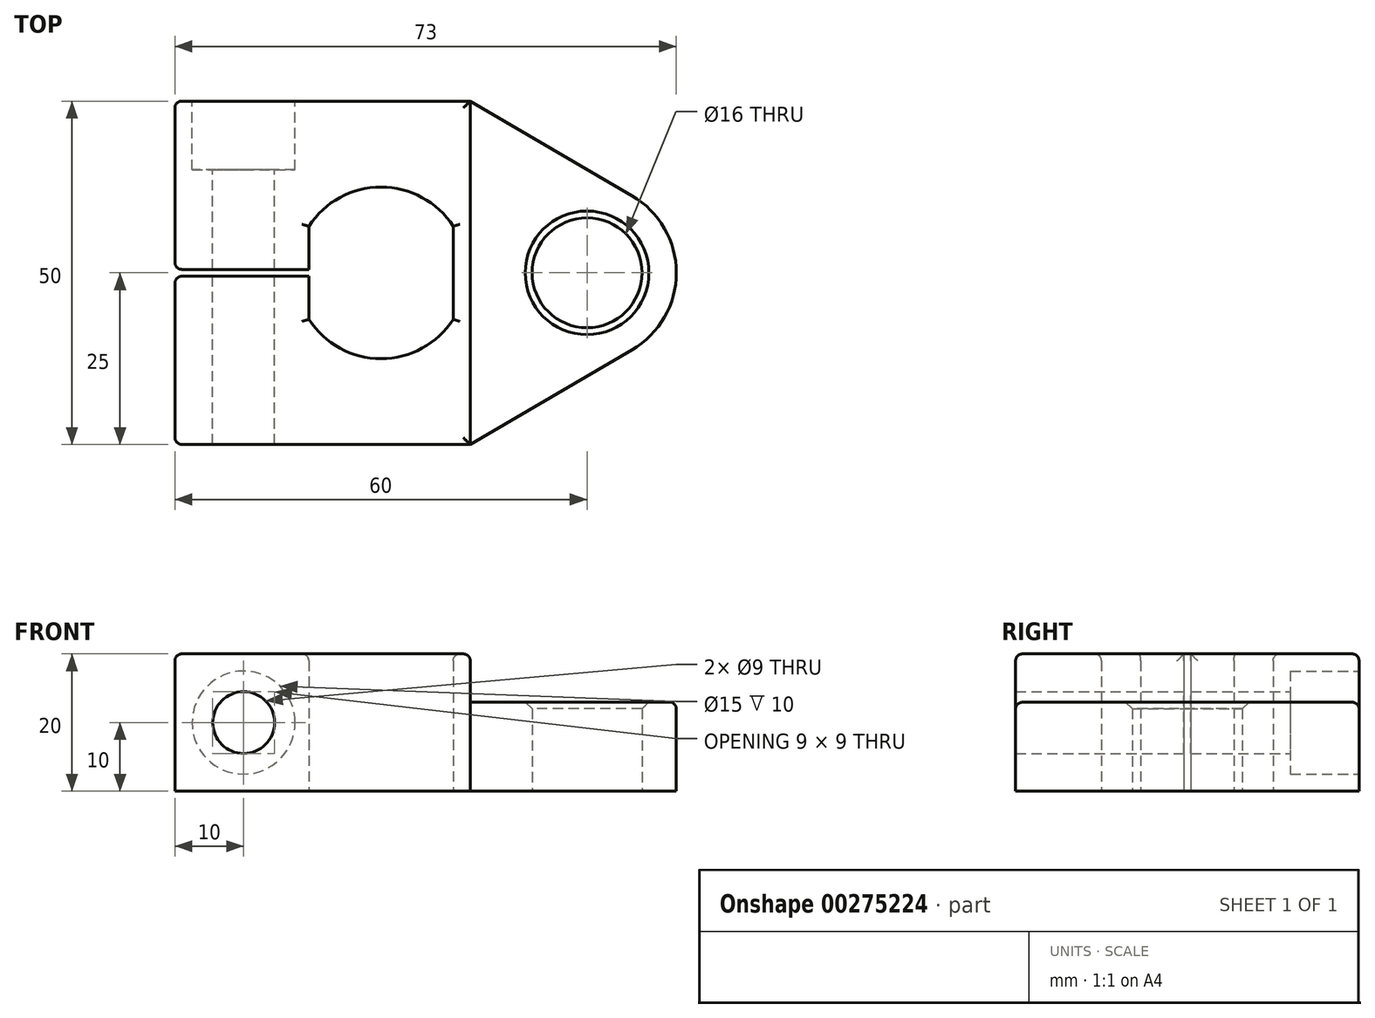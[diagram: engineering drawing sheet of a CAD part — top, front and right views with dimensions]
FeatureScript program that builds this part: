
annotation { "Feature Type Name" : "Feature", "Feature Type Description" : "" }
export const myFeature = defineFeature(function(context is Context, id is Id, definition is map)
    precondition{}
    {
        {
            var Q0;
            Q0=qCreatedBy(makeId("Top.planeOp"),FACE);
            var sketch = newSketch(context, id + "F0", { "sketchPlane" : qUnion([Q0])});
            skLineSegment(sketch, "E0", {"start": v(0, 0) * mm, "end": v(43, 0) * mm});
            skLineSegment(sketch, "E1", {"start": v(0, 0) * mm, "end": v(0, 24.5) * mm});
            skLineSegment(sketch, "E2", {"start": v(0, 50) * mm, "end": v(43, 50) * mm});
            skLineSegment(sketch, "E3", {"start": v(43, 50) * mm, "end": v(66.56, 36.22) * mm});
            skLineSegment(sketch, "E4", {"start": v(43, 0) * mm, "end": v(66.56, 13.78) * mm});
            skCircle(sketch, "E5", {"center": v(60, 25) * mm, "radius": 8 * mm});
            skArc(sketch, "E6", {"start": v(66.56, 36.22) * mm, "mid": v(73, 25) * mm, "end": v(66.56, 13.78) * mm});
            skPoint(sketch, "E7", {"position": v(73, 25) * mm});
            skLineSegment(sketch, "E8", {"start": v(43, 50) * mm, "end": v(43, 0) * mm});
            skLineSegment(sketch, "E9", {"start": v(19.5, 31.78) * mm, "end": v(19.5, 25) * mm});
            skLineSegment(sketch, "E10", {"start": v(40.5, 31.78) * mm, "end": v(40.5, 18.22) * mm});
            skArc(sketch, "E11", {"start": v(40.5, 31.78) * mm, "mid": v(30, 37.5) * mm, "end": v(19.5, 31.78) * mm});
            skLineSegment(sketch, "E12", {"start": v(60, 25) * mm, "end": v(-29.37, 25) * mm, "construction": true});
            skArc(sketch, "E13.MirrorCS", {"start": v(40.5, 18.22) * mm, "mid": v(30, 12.5) * mm, "end": v(19.5, 18.22) * mm});
            skLineSegment(sketch, "E14", {"start": v(19.5, 25.5) * mm, "end": v(0, 25.5) * mm});
            skLineSegment(sketch, "E15.MirrorCS", {"start": v(19.5, 24.5) * mm, "end": v(0, 24.5) * mm});
            skLineSegment(sketch, "E16.trimOffspring", {"start": v(0, 25) * mm, "end": v(0, 50) * mm});
            skLineSegment(sketch, "E17.trimOffspring", {"start": v(19.5, 24.5) * mm, "end": v(19.5, 18.22) * mm});
            skSolve(sketch);
        }
        {
            var Q0;
            Q0=makeQuery(id+"F0.imprint","IMPRINT",FACE,{"disambiguationData":[TD([[makeQuery(id+"F0.imprint","IMPRINT",EDGE,{"derivedFrom":sQuery(id+"F0.wireOp",EDGE,"E3")}),-1.0]])]});
            extrude(context, id + "F1", {"entities" : qUnion([Q0]), "depth" : 13 * mm});
        }
        {
            var Q0;
            Q0=makeQuery(id+"F0.imprint","IMPRINT",FACE,{"disambiguationData":[TD([[makeQuery(id+"F0.imprint","IMPRINT",EDGE,{"derivedFrom":sQuery(id+"F0.wireOp",EDGE,"E0")}),1.0]])]});
            extrude(context, id + "F2", {"entities" : qUnion([Q0]), "operationType" : NewBodyOperationType.ADD, "depth" : 20 * mm});
        }
        {
            var Q0;
            Q0=makeQuery(id+"F2.opExtrude","SWEPT_FACE",FACE,{"disambiguationData":[OSD([sQuery(id+"F0.wireOp",EDGE,"E2")])]});
            var sketch = newSketch(context, id + "F3", { "sketchPlane" : qUnion([Q0])});
            skPoint(sketch, "E18", {"position": v(-10, 10) * mm});
            skSolve(sketch);
        }
        {
            var Q0;
            Q0=sQuery(id+"F3.wireOp",VERTEX,"E18");
            var Q1;
            Q1=makeQuery(id+"F1.opExtrude","SWEPT_BODY",BODY,{"disambiguationData":[OSD([sQuery(id+"F0.wireOp",EDGE,"E3"),sQuery(id+"F0.wireOp",EDGE,"E4"),sQuery(id+"F0.wireOp",EDGE,"E5"),sQuery(id+"F0.wireOp",EDGE,"E6"),sQuery(id+"F0.wireOp",EDGE,"E8")])]});
            hole(context, id + "F4", {"style" : HoleStyle.C_BORE, "endStyle" : HoleEndStyle.THROUGH, "holeDiameter" : 9 * mm, "cBoreDiameter" : 15 * mm, "cBoreDepth" : 10 * mm, "tappedDepth" : 12 * mm, "tapClearance" : 3, "locations" : qUnion([Q0]), "scope" : qUnion([Q1])});
        }
        {
            var Q0;
            Q0=makeQuery(id+"F2.opExtrude","SWEPT_EDGE",EDGE,{"disambiguationData":[OSD([sQuery(id+"F0.wireOp",EDGE,"E0"),sQuery(id+"F0.wireOp",EDGE,"E1")])]});
            var Q1;
            Q1=makeQuery(id+"F2.opExtrude","CAP_EDGE",EDGE,{"disambiguationData":[OSD([sQuery(id+"F0.wireOp",EDGE,"E2")])],"isStart":false});
            var Q2;
            Q2=makeQuery(id+"F2.opExtrude","CAP_EDGE",EDGE,{"disambiguationData":[OSD([sQuery(id+"F0.wireOp",EDGE,"E16.trimOffspring")])],"isStart":false});
            var Q3;
            Q3=makeQuery(id+"F2.opExtrude","CAP_EDGE",EDGE,{"disambiguationData":[OSD([sQuery(id+"F0.wireOp",EDGE,"E0")])],"isStart":false});
            var Q4;
            Q4=makeQuery(id+"F2.opExtrude","CAP_EDGE",EDGE,{"disambiguationData":[OSD([sQuery(id+"F0.wireOp",EDGE,"E8")])],"isStart":false});
            var Q5;
            Q5=makeQuery(id+"F2.opExtrude","CAP_EDGE",EDGE,{"disambiguationData":[OSD([sQuery(id+"F0.wireOp",EDGE,"E11")])],"isStart":false});
            var Q6;
            Q6=makeQuery(id+"F2.opExtrude","CAP_EDGE",EDGE,{"disambiguationData":[OSD([sQuery(id+"F0.wireOp",EDGE,"E13.MirrorCS")])],"isStart":false});
            var Q7;
            Q7=makeQuery(id+"F2.opExtrude","CAP_EDGE",EDGE,{"disambiguationData":[OSD([sQuery(id+"F0.wireOp",EDGE,"E10")])],"isStart":false});
            var Q8;
            Q8=makeQuery(id+"F2.opExtrude","CAP_EDGE",EDGE,{"disambiguationData":[OSD([sQuery(id+"F0.wireOp",EDGE,"E17.trimOffspring")])],"isStart":false});
            var Q9;
            Q9=makeQuery(id+"F2.opExtrude","CAP_EDGE",EDGE,{"disambiguationData":[OSD([sQuery(id+"F0.wireOp",EDGE,"E9")])],"isStart":false});
            var Q10;
            Q10=makeQuery(id+"F2.opExtrude","SWEPT_EDGE",EDGE,{"disambiguationData":[OSD([sQuery(id+"F0.wireOp",EDGE,"E14"),sQuery(id+"F0.wireOp",EDGE,"E16.trimOffspring")])]});
            var Q11;
            Q11=makeQuery(id+"F1.opExtrude","CAP_EDGE",EDGE,{"disambiguationData":[OSD([sQuery(id+"F0.wireOp",EDGE,"E4")])],"isStart":false});
            var Q12;
            Q12=makeQuery(id+"F2.opExtrude","CAP_EDGE",EDGE,{"disambiguationData":[OSD([sQuery(id+"F0.wireOp",EDGE,"E1")])],"isStart":false});
            var Q13;
            Q13=makeQuery(id+"F2.opExtrude","SWEPT_EDGE",EDGE,{"disambiguationData":[OSD([sQuery(id+"F0.wireOp",EDGE,"E1"),sQuery(id+"F0.wireOp",EDGE,"E15.MirrorCS")])]});
            var Q14;
            Q14=makeQuery(id+"F2.opExtrude","SWEPT_EDGE",EDGE,{"disambiguationData":[OSD([sQuery(id+"F0.wireOp",EDGE,"E2"),sQuery(id+"F0.wireOp",EDGE,"E16.trimOffspring")])]});
            fillet(context, id + "F5", {"entities" : qUnion([Q0, Q1, Q2, Q3, Q4, Q5, Q6, Q7, Q8, Q9, Q10, Q11, Q12, Q13, Q14]), "radius" : 1 * mm, "tangentPropagation" : true, "allowEdgeOverflow" : false});
        }
        {
            var Q0;
            Q0=makeQuery(id+"F1.opExtrude","CAP_EDGE",EDGE,{"disambiguationData":[OSD([sQuery(id+"F0.wireOp",EDGE,"E5")])],"isStart":false});
            var Q1;
            Q1=makeQuery(id+"F4.hole-0.boolean.opBoolean","COPY",EDGE,{"derivedFrom":makeQuery(id+"F4.hole-0.opRevolve","SWEPT_EDGE",EDGE,{"disambiguationData":[OSD([sQuery(id+"F4.hole-0.sketch.wireOp",EDGE,"cbore_start_line_2"),sQuery(id+"F4.hole-0.sketch.wireOp",EDGE,"cbore_start_line_3")])]})});
            chamfer(context, id + "F6", {"entities" : qUnion([Q0, Q1]), "chamferType" : ChamferType.OFFSET_ANGLE, "width" : 1 * mm, "oppositeDirection" : false, "angle" : 45 * degree, "tangentPropagation" : true});
        }
    });
